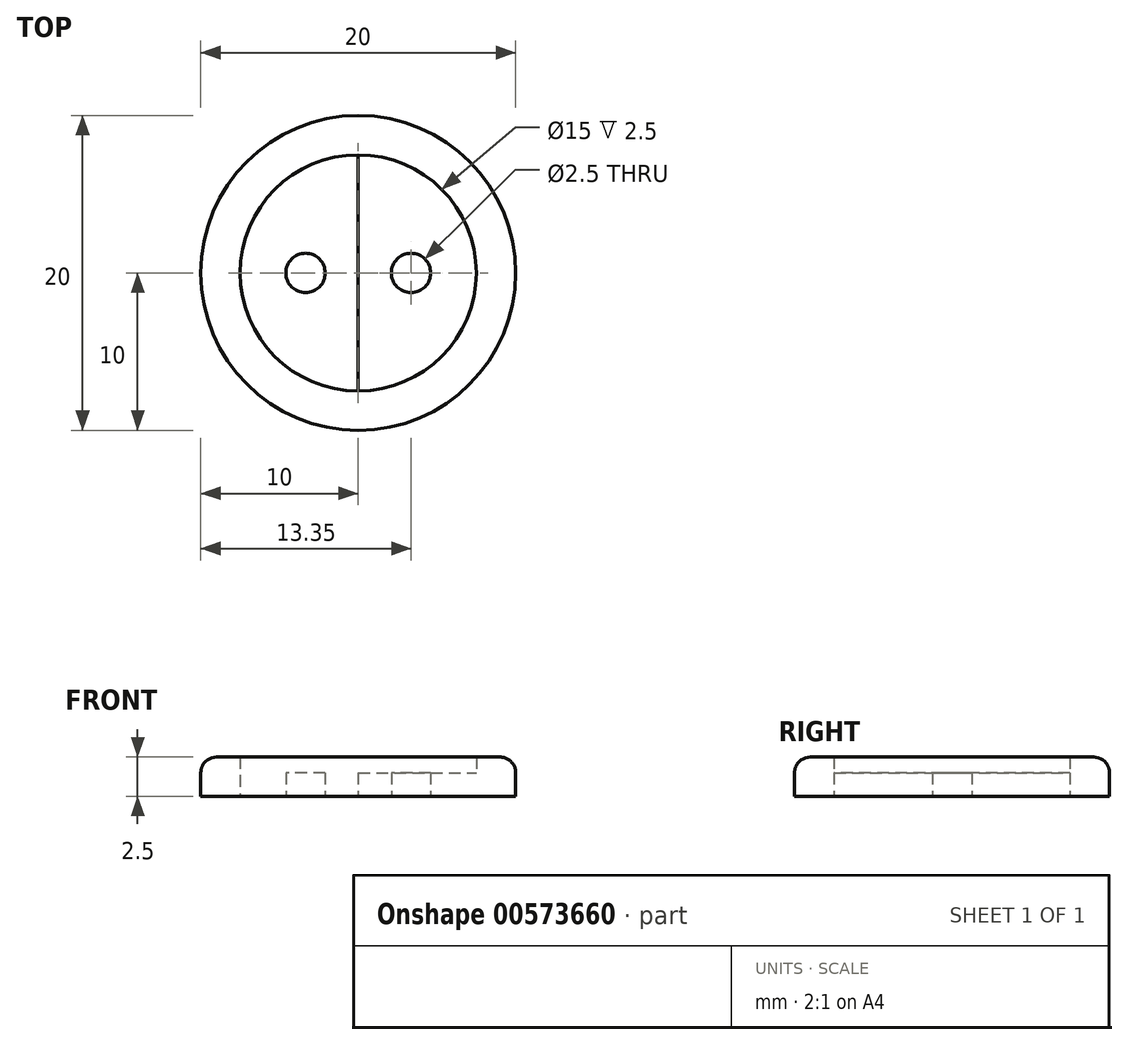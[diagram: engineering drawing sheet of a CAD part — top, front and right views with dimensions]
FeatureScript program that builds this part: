
annotation { "Feature Type Name" : "Feature", "Feature Type Description" : "" }
export const myFeature = defineFeature(function(context is Context, id is Id, definition is map)
    precondition{}
    {
        {
            var Q0;
            Q0=qCreatedBy(makeId("Top.planeOp"),FACE);
            var sketch = newSketch(context, id + "F0", { "sketchPlane" : qUnion([Q0])});
            skCircle(sketch, "E0", {"center": v(0, 0) * mm, "radius": 7.5 * mm});
            skCircle(sketch, "E1", {"center": v(0, 0) * mm, "radius": 10 * mm});
            skLineSegment(sketch, "E2", {"start": v(0, 38.11) * mm, "end": v(0, -48.24) * mm});
            skCircle(sketch, "E3", {"center": v(3.35, 0) * mm, "radius": 1.25 * mm});
            skCircle(sketch, "E4.MirrorC", {"center": v(-3.35, 0) * mm, "radius": 1.25 * mm});
            skSolve(sketch);
        }
        {
            var Q0;
            Q0=qSketchRegion(id+"F0",true);
            extrude(context, id + "F1", {"entities" : qUnion([Q0]), "depth" : 2.5 * mm, "offsetDistance" : 25 * mm});
        }
        {
            var Q0;
            Q0=makeQuery(id+"F0.imprint","IMPRINT",FACE,{"disambiguationData":[TD([[makeQuery(id+"F0.imprint","IMPRINT",EDGE,{"derivedFrom":sQuery(id+"F0.wireOp",EDGE,"E4.MirrorC")}),1.0]])]});
            var Q1;
            Q1=makeQuery(id+"F0.imprint","IMPRINT",FACE,{"disambiguationData":[TD([[makeQuery(id+"F0.imprint","IMPRINT",EDGE,{"derivedFrom":sQuery(id+"F0.wireOp",EDGE,"E3")}),-1.0]])]});
            extrude(context, id + "F2", {"entities" : qUnion([Q0, Q1]), "operationType" : NewBodyOperationType.ADD, "depth" : 1.5 * mm, "offsetDistance" : 25 * mm});
        }
        {
            var Q0;
            Q0=makeQuery(id+"F1.opExtrude","CAP_EDGE",EDGE,{"disambiguationData":[OSD([sQuery(id+"F0.wireOp",EDGE,"E1")])],"isStart":false});
            fillet(context, id + "F3", {"entities" : qUnion([Q0]), "radius" : 1 * mm, "tangentPropagation" : true, "allowEdgeOverflow" : false});
        }
    });
